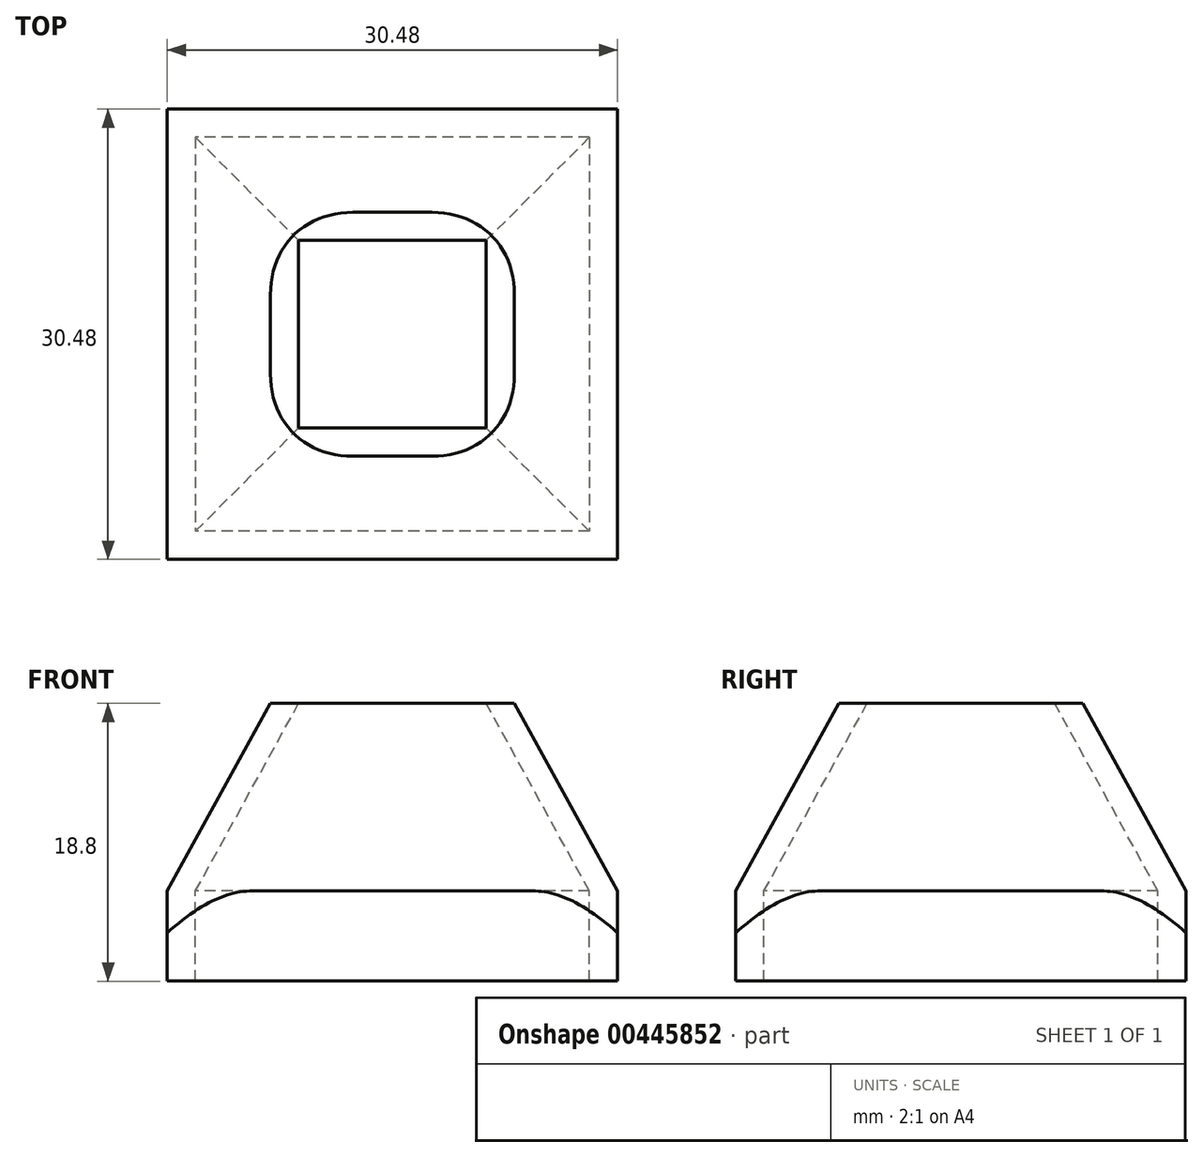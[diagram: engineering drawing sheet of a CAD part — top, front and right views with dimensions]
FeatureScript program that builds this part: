
annotation { "Feature Type Name" : "Feature", "Feature Type Description" : "" }
export const myFeature = defineFeature(function(context is Context, id is Id, definition is map)
    precondition{}
    {
        {
            var Q0;
            Q0=qCreatedBy(makeId("Top.planeOp"),FACE);
            var sketch = newSketch(context, id + "F0", { "sketchPlane" : qUnion([Q0])});
            skLineSegment(sketch, "E0.bottom", {"start": v(13.33, 13.34) * mm, "end": v(-13.34, 13.34) * mm});
            skLineSegment(sketch, "E0.top", {"start": v(13.34, -13.34) * mm, "end": v(-13.33, -13.34) * mm});
            skLineSegment(sketch, "E0.left", {"start": v(13.33, 13.34) * mm, "end": v(13.34, -13.34) * mm});
            skLineSegment(sketch, "E0.right", {"start": v(-13.34, 13.34) * mm, "end": v(-13.33, -13.34) * mm});
            skPoint(sketch, "E0.middle", {"position": v(0, 0) * mm});
            skLineSegment(sketch, "E1.0", {"start": v(15.24, -15.24) * mm, "end": v(-15.24, -15.24) * mm});
            skLineSegment(sketch, "E1.1", {"start": v(15.24, 15.24) * mm, "end": v(15.24, -15.24) * mm});
            skLineSegment(sketch, "E1.2", {"start": v(15.24, 15.24) * mm, "end": v(-15.24, 15.24) * mm});
            skLineSegment(sketch, "E1.3", {"start": v(-15.24, 15.24) * mm, "end": v(-15.24, -15.24) * mm});
            skSolve(sketch);
        }
        {
            var Q0;
            Q0=makeQuery(id+"F0.imprint","IMPRINT",FACE,{"disambiguationData":[TD([[makeQuery(id+"F0.imprint","IMPRINT",EDGE,{"derivedFrom":sQuery(id+"F0.wireOp",EDGE,"E0.bottom")}),-1.0]])]});
            extrude(context, id + "F1", {"entities" : qUnion([Q0]), "oppositeDirection" : true, "depth" : 2.3 * mm});
        }
        {
            var Q0;
            Q0=makeQuery(id+"F0.imprint","IMPRINT",FACE,{"disambiguationData":[TD([[makeQuery(id+"F0.imprint","IMPRINT",EDGE,{"derivedFrom":sQuery(id+"F0.wireOp",EDGE,"E0.bottom")}),-1.0]])]});
            extrude(context, id + "F2", {"entities" : qUnion([Q0]), "operationType" : NewBodyOperationType.ADD, "depth" : 3.8 * mm});
        }
        {
            var Q0;
            Q0=makeQuery(id+"F2.opExtrude","CAP_FACE",FACE,{"disambiguationData":[OSD([sQuery(id+"F0.wireOp",EDGE,"E0.bottom"),sQuery(id+"F0.wireOp",EDGE,"E0.top"),sQuery(id+"F0.wireOp",EDGE,"E0.left"),sQuery(id+"F0.wireOp",EDGE,"E0.right"),sQuery(id+"F0.wireOp",EDGE,"E1.0"),sQuery(id+"F0.wireOp",EDGE,"E1.1"),sQuery(id+"F0.wireOp",EDGE,"E1.2"),sQuery(id+"F0.wireOp",EDGE,"E1.3")])],"isStart":false});
            cPlane(context, id + "F3", {"entities" : qUnion([Q0]), "cplaneType" : CPlaneType.OFFSET, "offset" : 12.7 * mm, "width" : 152.4 * mm, "height" : 152.4 * mm});
        }
        {
            var Q0;
            Q0=qCreatedBy(id+"F3.planeOp",FACE);
            var sketch = newSketch(context, id + "F4", { "sketchPlane" : qUnion([Q0])});
            skLineSegment(sketch, "E2.bottom", {"start": v(6.35, 6.35) * mm, "end": v(-6.35, 6.35) * mm});
            skLineSegment(sketch, "E2.top", {"start": v(6.35, -6.35) * mm, "end": v(-6.35, -6.35) * mm});
            skLineSegment(sketch, "E2.left", {"start": v(6.35, 6.35) * mm, "end": v(6.35, -6.35) * mm});
            skLineSegment(sketch, "E2.right", {"start": v(-6.35, 6.35) * mm, "end": v(-6.35, -6.35) * mm});
            skPoint(sketch, "E2.middle", {"position": v(0, 0) * mm});
            skLineSegment(sketch, "E3.0", {"start": v(8.26, -8.26) * mm, "end": v(-8.26, -8.26) * mm});
            skLineSegment(sketch, "E3.1", {"start": v(8.26, 8.25) * mm, "end": v(8.26, -8.26) * mm});
            skLineSegment(sketch, "E3.2", {"start": v(8.26, 8.25) * mm, "end": v(-8.26, 8.26) * mm});
            skLineSegment(sketch, "E3.3", {"start": v(-8.26, 8.26) * mm, "end": v(-8.26, -8.26) * mm});
            skLineSegment(sketch, "E4", {"start": v(-6.35, -6.35) * mm, "end": v(-8.26, -8.26) * mm});
            skLineSegment(sketch, "E5", {"start": v(-6.35, 6.35) * mm, "end": v(-8.26, 8.26) * mm});
            skLineSegment(sketch, "E6", {"start": v(6.35, -6.35) * mm, "end": v(8.26, -8.26) * mm});
            skLineSegment(sketch, "E7", {"start": v(6.35, 6.35) * mm, "end": v(8.26, 8.25) * mm});
            skSolve(sketch);
        }
        {
            var Q0;
            Q0=makeQuery(id+"F2.opExtrude","CAP_FACE",FACE,{"disambiguationData":[OSD([sQuery(id+"F0.wireOp",EDGE,"E0.bottom"),sQuery(id+"F0.wireOp",EDGE,"E0.top"),sQuery(id+"F0.wireOp",EDGE,"E0.left"),sQuery(id+"F0.wireOp",EDGE,"E0.right"),sQuery(id+"F0.wireOp",EDGE,"E1.0"),sQuery(id+"F0.wireOp",EDGE,"E1.1"),sQuery(id+"F0.wireOp",EDGE,"E1.2"),sQuery(id+"F0.wireOp",EDGE,"E1.3")])],"isStart":false});
            var sketch = newSketch(context, id + "F5", { "sketchPlane" : qUnion([Q0])});
            skLineSegment(sketch, "E8.0.0", {"start": v(15.24, 15.24) * mm, "end": v(-15.24, 15.24) * mm});
            skLineSegment(sketch, "E8.0.1", {"start": v(-15.24, 15.24) * mm, "end": v(-15.24, -15.24) * mm});
            skLineSegment(sketch, "E8.0.2", {"start": v(-15.24, -15.24) * mm, "end": v(15.24, -15.24) * mm});
            skLineSegment(sketch, "E8.0.3", {"start": v(15.24, -15.24) * mm, "end": v(15.24, 15.24) * mm});
            skLineSegment(sketch, "E9.0", {"start": v(13.34, -13.34) * mm, "end": v(-13.33, -13.34) * mm});
            skLineSegment(sketch, "E10.0", {"start": v(-13.34, 13.34) * mm, "end": v(-13.33, -13.34) * mm});
            skLineSegment(sketch, "E11.0", {"start": v(13.33, 13.34) * mm, "end": v(13.34, -13.34) * mm});
            skLineSegment(sketch, "E12.0", {"start": v(13.33, 13.34) * mm, "end": v(-13.34, 13.34) * mm});
            skLineSegment(sketch, "E13", {"start": v(-15.24, -15.24) * mm, "end": v(-13.33, -13.34) * mm});
            skLineSegment(sketch, "E14", {"start": v(-15.24, 15.24) * mm, "end": v(-13.34, 13.34) * mm});
            skLineSegment(sketch, "E15", {"start": v(15.24, -15.24) * mm, "end": v(13.34, -13.34) * mm});
            skLineSegment(sketch, "E16", {"start": v(15.24, 15.24) * mm, "end": v(13.33, 13.34) * mm});
            skSolve(sketch);
        }
        {
            var Q1;
            Q1=makeQuery(id+"F5.imprint","IMPRINT",FACE,{"disambiguationData":[TD([[makeQuery(id+"F5.imprint","IMPRINT",EDGE,{"derivedFrom":sQuery(id+"F5.wireOp",EDGE,"E8.0.1")}),1.0]])]});
            var Q2;
            Q2=makeQuery(id+"F4.imprint","IMPRINT",FACE,{"disambiguationData":[TD([[makeQuery(id+"F4.imprint","IMPRINT",EDGE,{"derivedFrom":sQuery(id+"F4.wireOp",EDGE,"E2.right")}),-1.0]])]});
            loft(context, id + "F6", {"operationType" : NewBodyOperationType.ADD, "sheetProfilesArray" : [{ "sheetProfileEntities" : qUnion([Q1]) }, { "sheetProfileEntities" : qUnion([Q2]) }]});
        }
        {
            var Q1;
            Q1=makeQuery(id+"F5.imprint","IMPRINT",FACE,{"disambiguationData":[TD([[makeQuery(id+"F5.imprint","IMPRINT",EDGE,{"derivedFrom":sQuery(id+"F5.wireOp",EDGE,"E8.0.2")}),-1.0]])]});
            var Q2;
            Q2=makeQuery(id+"F4.imprint","IMPRINT",FACE,{"disambiguationData":[TD([[makeQuery(id+"F4.imprint","IMPRINT",EDGE,{"derivedFrom":sQuery(id+"F4.wireOp",EDGE,"E2.top")}),1.0]])]});
            loft(context, id + "F7", {"operationType" : NewBodyOperationType.ADD, "sheetProfilesArray" : [{ "sheetProfileEntities" : qUnion([Q1]) }, { "sheetProfileEntities" : qUnion([Q2]) }]});
        }
        {
            var Q1;
            Q1=makeQuery(id+"F5.imprint","IMPRINT",FACE,{"disambiguationData":[TD([[makeQuery(id+"F5.imprint","IMPRINT",EDGE,{"derivedFrom":sQuery(id+"F5.wireOp",EDGE,"E8.0.3")}),-1.0]])]});
            var Q2;
            Q2=makeQuery(id+"F4.imprint","IMPRINT",FACE,{"disambiguationData":[TD([[makeQuery(id+"F4.imprint","IMPRINT",EDGE,{"derivedFrom":sQuery(id+"F4.wireOp",EDGE,"E2.left")}),1.0]])]});
            loft(context, id + "F8", {"operationType" : NewBodyOperationType.ADD, "sheetProfilesArray" : [{ "sheetProfileEntities" : qUnion([Q1]) }, { "sheetProfileEntities" : qUnion([Q2]) }]});
        }
        {
            var Q1;
            Q1=makeQuery(id+"F5.imprint","IMPRINT",FACE,{"disambiguationData":[TD([[makeQuery(id+"F5.imprint","IMPRINT",EDGE,{"derivedFrom":sQuery(id+"F5.wireOp",EDGE,"E8.0.0")}),1.0]])]});
            var Q2;
            Q2=makeQuery(id+"F4.imprint","IMPRINT",FACE,{"disambiguationData":[TD([[makeQuery(id+"F4.imprint","IMPRINT",EDGE,{"derivedFrom":sQuery(id+"F4.wireOp",EDGE,"E2.bottom")}),-1.0]])]});
            loft(context, id + "F9", {"operationType" : NewBodyOperationType.ADD, "sheetProfilesArray" : [{ "sheetProfileEntities" : qUnion([Q1]) }, { "sheetProfileEntities" : qUnion([Q2]) }]});
        }
        {
            var Q0;
            {var subQ0=sQuery(id+"F5.wireOp",EDGE,"E13");var subQ1=sQuery(id+"F5.wireOp",EDGE,"E8.0.2");var subQ2=sQuery(id+"F5.wireOp",EDGE,"E8.0.1");var subQ3=sQuery(id+"F4.wireOp",EDGE,"E4");var subQ4=sQuery(id+"F4.wireOp",EDGE,"E3.3");var subQ5=sQuery(id+"F4.wireOp",EDGE,"E3.0");Q0=makeQuery(id+"F7.boolean.opBoolean","MERGE",EDGE,{"derivedFrom":[makeQuery(id+"F6.opLoft","SWEPT_EDGE",EDGE,{"disambiguationData":[OSD([subQ5,subQ4,subQ3,subQ2,subQ1,subQ0])]}),makeQuery(id+"F7.opLoft","SWEPT_EDGE",EDGE,{"disambiguationData":[OSD([subQ5,subQ4,subQ3,subQ2,subQ1,subQ0])]})]});}
            var Q1;
            {var subQ0=sQuery(id+"F5.wireOp",EDGE,"E15");var subQ1=sQuery(id+"F5.wireOp",EDGE,"E8.0.3");var subQ2=sQuery(id+"F5.wireOp",EDGE,"E8.0.2");var subQ3=sQuery(id+"F4.wireOp",EDGE,"E6");var subQ4=sQuery(id+"F4.wireOp",EDGE,"E3.1");var subQ5=sQuery(id+"F4.wireOp",EDGE,"E3.0");Q1=makeQuery(id+"F8.boolean.opBoolean","MERGE",EDGE,{"derivedFrom":[makeQuery(id+"F7.opLoft","SWEPT_EDGE",EDGE,{"disambiguationData":[OSD([subQ5,subQ4,subQ3,subQ2,subQ1,subQ0])]}),makeQuery(id+"F8.opLoft","SWEPT_EDGE",EDGE,{"disambiguationData":[OSD([subQ5,subQ4,subQ3,subQ2,subQ1,subQ0])]})]});}
            var Q2;
            {var subQ0=sQuery(id+"F5.wireOp",EDGE,"E16");var subQ1=sQuery(id+"F5.wireOp",EDGE,"E8.0.3");var subQ2=sQuery(id+"F5.wireOp",EDGE,"E8.0.0");var subQ3=sQuery(id+"F4.wireOp",EDGE,"E7");var subQ4=sQuery(id+"F4.wireOp",EDGE,"E3.2");var subQ5=sQuery(id+"F4.wireOp",EDGE,"E3.1");Q2=makeQuery(id+"F9.boolean.opBoolean","MERGE",EDGE,{"derivedFrom":[makeQuery(id+"F8.opLoft","SWEPT_EDGE",EDGE,{"disambiguationData":[OSD([subQ5,subQ4,subQ3,subQ2,subQ1,subQ0])]}),makeQuery(id+"F9.opLoft","SWEPT_EDGE",EDGE,{"disambiguationData":[OSD([subQ5,subQ4,subQ3,subQ2,subQ1,subQ0])]})]});}
            var Q3;
            {var subQ0=sQuery(id+"F5.wireOp",EDGE,"E14");var subQ1=sQuery(id+"F5.wireOp",EDGE,"E8.0.1");var subQ2=sQuery(id+"F5.wireOp",EDGE,"E8.0.0");var subQ3=sQuery(id+"F4.wireOp",EDGE,"E5");var subQ4=sQuery(id+"F4.wireOp",EDGE,"E3.3");var subQ5=sQuery(id+"F4.wireOp",EDGE,"E3.2");Q3=makeQuery(id+"F9.boolean.opBoolean","MERGE",EDGE,{"derivedFrom":[makeQuery(id+"F6.opLoft","SWEPT_EDGE",EDGE,{"disambiguationData":[OSD([subQ5,subQ4,subQ3,subQ2,subQ1,subQ0])]}),makeQuery(id+"F9.opLoft","SWEPT_EDGE",EDGE,{"disambiguationData":[OSD([subQ5,subQ4,subQ3,subQ2,subQ1,subQ0])]})]});}
            fillet(context, id + "F10", {"entities" : qUnion([Q0, Q1, Q2, Q3]), "radius" : 6.35 * mm, "tangentPropagation" : true, "allowEdgeOverflow" : false});
        }
    });
